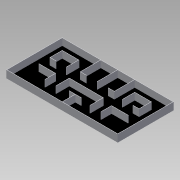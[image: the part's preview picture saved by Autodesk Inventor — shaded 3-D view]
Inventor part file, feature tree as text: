
AUTODESK INVENTOR PART (.ipt)
format: ipt  version: 2015 SP1 (Build 190203100, 203)  size: 308,224 bytes
history: native  units: mm
features: extrude x3, sketch x2
ambient origin geometry x8: Origin, YZ Plane, XZ Plane, XY Plane, X Axis, Y Axis, Z Axis, Center Point
bodies: Solid1 (feature_tree)
feature tree (5):
  sketch  "Sketch1"  dims[d2=20.0mm d51=460.0mm d52=460.0mm]
  extrude  "Extrusion1"  Depth=460.0mm
  extrude  "Extrusion2"  Depth=320.0mm TaperAngle=0.0deg
  sketch  "Sketch5"  dims[d97=20.0mm d98=0.0mm d99=320.0mm d100=0.0mm d190=20.0mm d191=300.0mm d192=0.0mm d193=20.0mm d194=460.0mm d274=4860.0mm d275=2440.0mm d276=2400.0mm d277=2400.0mm d278=720.0mm d279=450.0mm d280=20.0mm d281=470.0mm d282=740.0mm d283=20.0mm d284=700.0mm d285=510.0mm d286=260.0mm d287=20.0mm d288=280.0mm d289=550.0mm d290=740.0mm d291=550.0mm d292=20.0mm d293=530.0mm d294=890.0mm d295=280.0mm d296=20.0mm d297=260.0mm d298=870.0mm d300=870.0mm d301=20.0mm d302=550.0mm d303=260.0mm d304=20.0mm d305=540.0mm d306=570.0mm d307=20.0mm d308=590.0mm d309=1500.0mm d310=1460.0mm d311=2400.0mm d312=20.0mm d313=20.0mm d314=20.0mm d315=20.0mm d316=20.0mm d318=1660.0mm d319=20.0mm d320=720.0mm d324=20.0mm d330=720.0mm d331=740.0mm d332=470.0mm d333=20.0mm d334=20.0mm d336=530.0mm d337=510.0mm d338=260.0mm d339=20.0mm d341=550.0mm d343=550.0mm d346=870.0mm d352=460.0mm d353=460.0mm d356=460.0mm d358=460.0mm d359=460.0mm d364=460.0mm d365=460.0mm d366=460.0mm d367=460.0mm d368=460.0mm d369=480.0mm d370=460.0mm d371=460.0mm d372=460.0mm d374=910.0mm]
  extrude  "Extrusion5"  Depth=20.0mm
